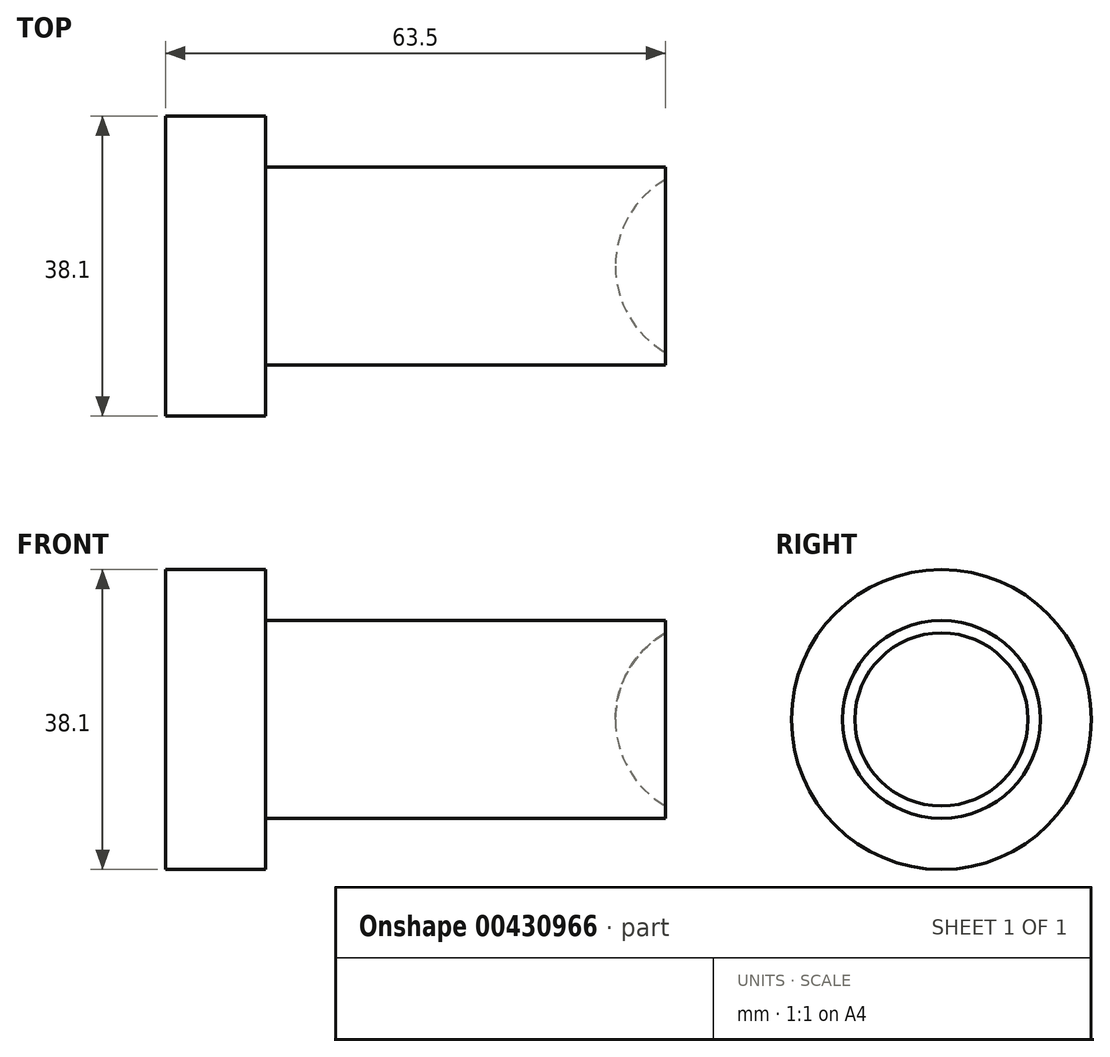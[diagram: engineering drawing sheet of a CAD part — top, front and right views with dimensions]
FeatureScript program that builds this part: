
annotation { "Feature Type Name" : "Feature", "Feature Type Description" : "" }
export const myFeature = defineFeature(function(context is Context, id is Id, definition is map)
    precondition{}
    {
        {
            var Q0;
            Q0=qCreatedBy(makeId("Front.planeOp"),FACE);
            var sketch = newSketch(context, id + "F0", { "sketchPlane" : qUnion([Q0])});
            skLineSegment(sketch, "E0.bottom", {"start": v(0, 0) * mm, "end": v(-12.7, 0) * mm});
            skLineSegment(sketch, "E0.top", {"start": v(0, 19.05) * mm, "end": v(-12.7, 19.05) * mm});
            skLineSegment(sketch, "E0.left", {"start": v(0, 0) * mm, "end": v(0, 19.05) * mm});
            skLineSegment(sketch, "E0.right", {"start": v(-12.7, 0) * mm, "end": v(-12.7, 19.05) * mm});
            skLineSegment(sketch, "E1.bottom", {"start": v(0, 0) * mm, "end": v(50.8, 0) * mm});
            skLineSegment(sketch, "E1.top", {"start": v(0, 12.57) * mm, "end": v(50.8, 12.57) * mm});
            skLineSegment(sketch, "E1.left", {"start": v(0, 0) * mm, "end": v(0, 12.57) * mm});
            skLineSegment(sketch, "E1.right", {"start": v(50.8, 0) * mm, "end": v(50.8, 12.57) * mm});
            skSolve(sketch);
        }
        {
            var Q0;
            Q0=makeQuery(id+"F0.imprint","IMPRINT",FACE,{"disambiguationData":[TD([[makeQuery(id+"F0.imprint","IMPRINT",EDGE,{"derivedFrom":sQuery(id+"F0.wireOp",EDGE,"E0.bottom")}),-1.0]])]});
            var Q1;
            Q1=makeQuery(id+"F0.imprint","IMPRINT",FACE,{"disambiguationData":[TD([[makeQuery(id+"F0.imprint","IMPRINT",EDGE,{"derivedFrom":sQuery(id+"F0.wireOp",EDGE,"E1.bottom")}),1.0]])]});
            var Q2;
            Q2=sQuery(id+"F0.wireOp",EDGE,"E0.bottom");
            revolve(context, id + "F1", {"entities" : qUnion([Q0, Q1]), "axis" : qUnion([Q2]), "revolveType" : RevolveType.FULL});
        }
        {
            var Q0;
            Q0=qCreatedBy(makeId("Front.planeOp"),FACE);
            var sketch = newSketch(context, id + "F2", { "sketchPlane" : qUnion([Q0])});
            skLineSegment(sketch, "E2", {"start": v(57.15, 12.7) * mm, "end": v(57.15, 0) * mm});
            skLineSegment(sketch, "E3", {"start": v(44.45, 0) * mm, "end": v(57.15, 0) * mm});
            skArc(sketch, "E4", {"start": v(57.15, 12.7) * mm, "mid": v(48.17, 8.98) * mm, "end": v(44.45, 0) * mm});
            skSolve(sketch);
        }
        {
            var Q0;
            Q0 = qSketchRegion(id + "F2", true);
            var Q1;
            Q1=sQuery(id+"F2.wireOp",EDGE,"E3");
            revolve(context, id + "F3", {"operationType" : NewBodyOperationType.REMOVE, "entities" : qUnion([Q0]), "axis" : qUnion([Q1]), "revolveType" : RevolveType.FULL, "oppositeDirection" : true});
        }
    });
